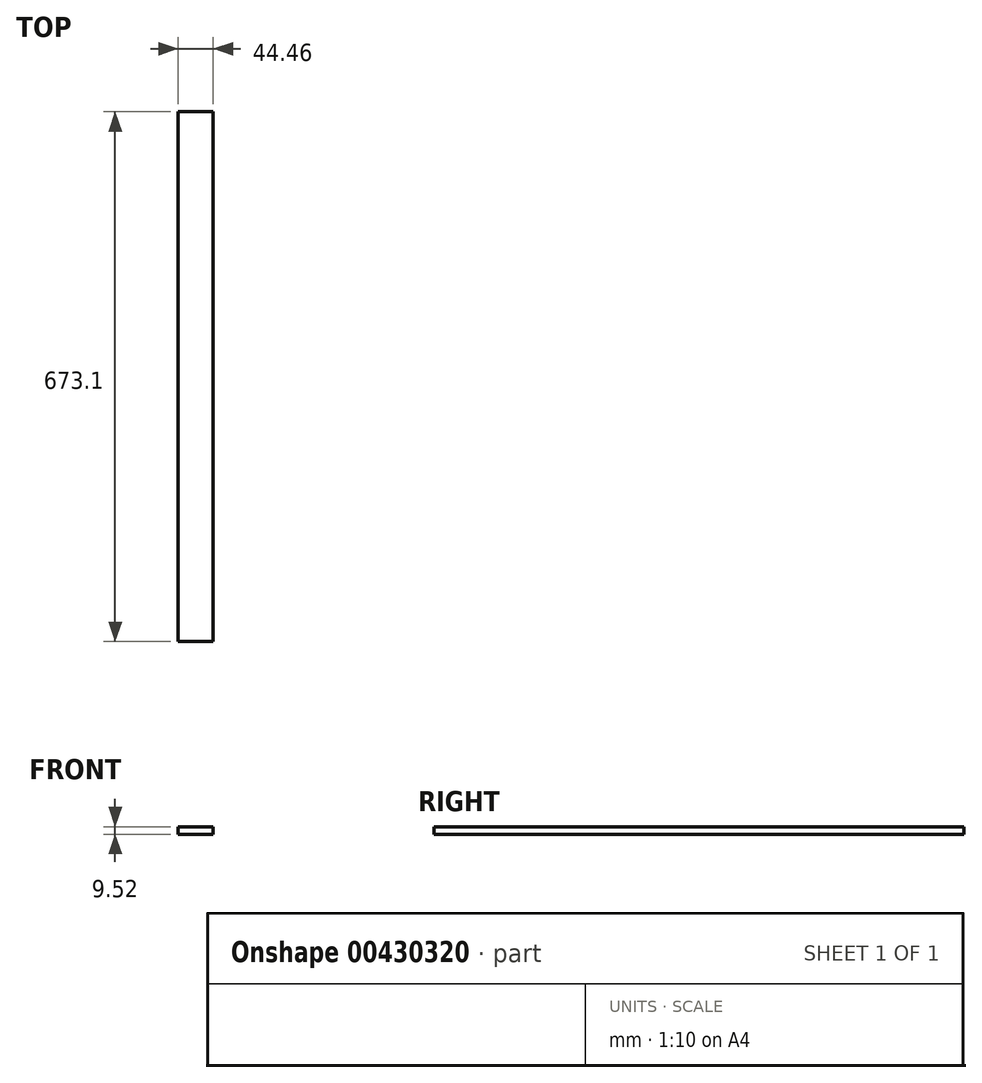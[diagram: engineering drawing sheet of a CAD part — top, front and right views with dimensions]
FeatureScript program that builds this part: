
annotation { "Feature Type Name" : "Feature", "Feature Type Description" : "" }
export const myFeature = defineFeature(function(context is Context, id is Id, definition is map)
    precondition{}
    {
        {
            var Q0;
            Q0=qCreatedBy(makeId("Front.planeOp"),FACE);
            var sketch = newSketch(context, id + "F0", { "sketchPlane" : qUnion([Q0])});
            skLineSegment(sketch, "E0.bottom", {"start": v(22.22, 4.76) * mm, "end": v(-22.23, 4.76) * mm});
            skLineSegment(sketch, "E0.top", {"start": v(22.22, -4.76) * mm, "end": v(-22.23, -4.76) * mm});
            skLineSegment(sketch, "E0.left", {"start": v(22.23, 4.76) * mm, "end": v(22.23, -4.76) * mm});
            skLineSegment(sketch, "E0.right", {"start": v(-22.23, 4.76) * mm, "end": v(-22.23, -4.76) * mm});
            skPoint(sketch, "E0.middle", {"position": v(0, 0) * mm});
            skSolve(sketch);
        }
        {
            var Q0;
            Q0=makeQuery(id+"F0.imprint","IMPRINT",FACE,{"disambiguationData":[TD([[makeQuery(id+"F0.imprint","IMPRINT",EDGE,{"derivedFrom":sQuery(id+"F0.wireOp",EDGE,"E0.bottom")}),1.0]])]});
            extrude(context, id + "F1", {"entities" : qUnion([Q0]), "depth" : 673.1 * mm});
        }
    });
